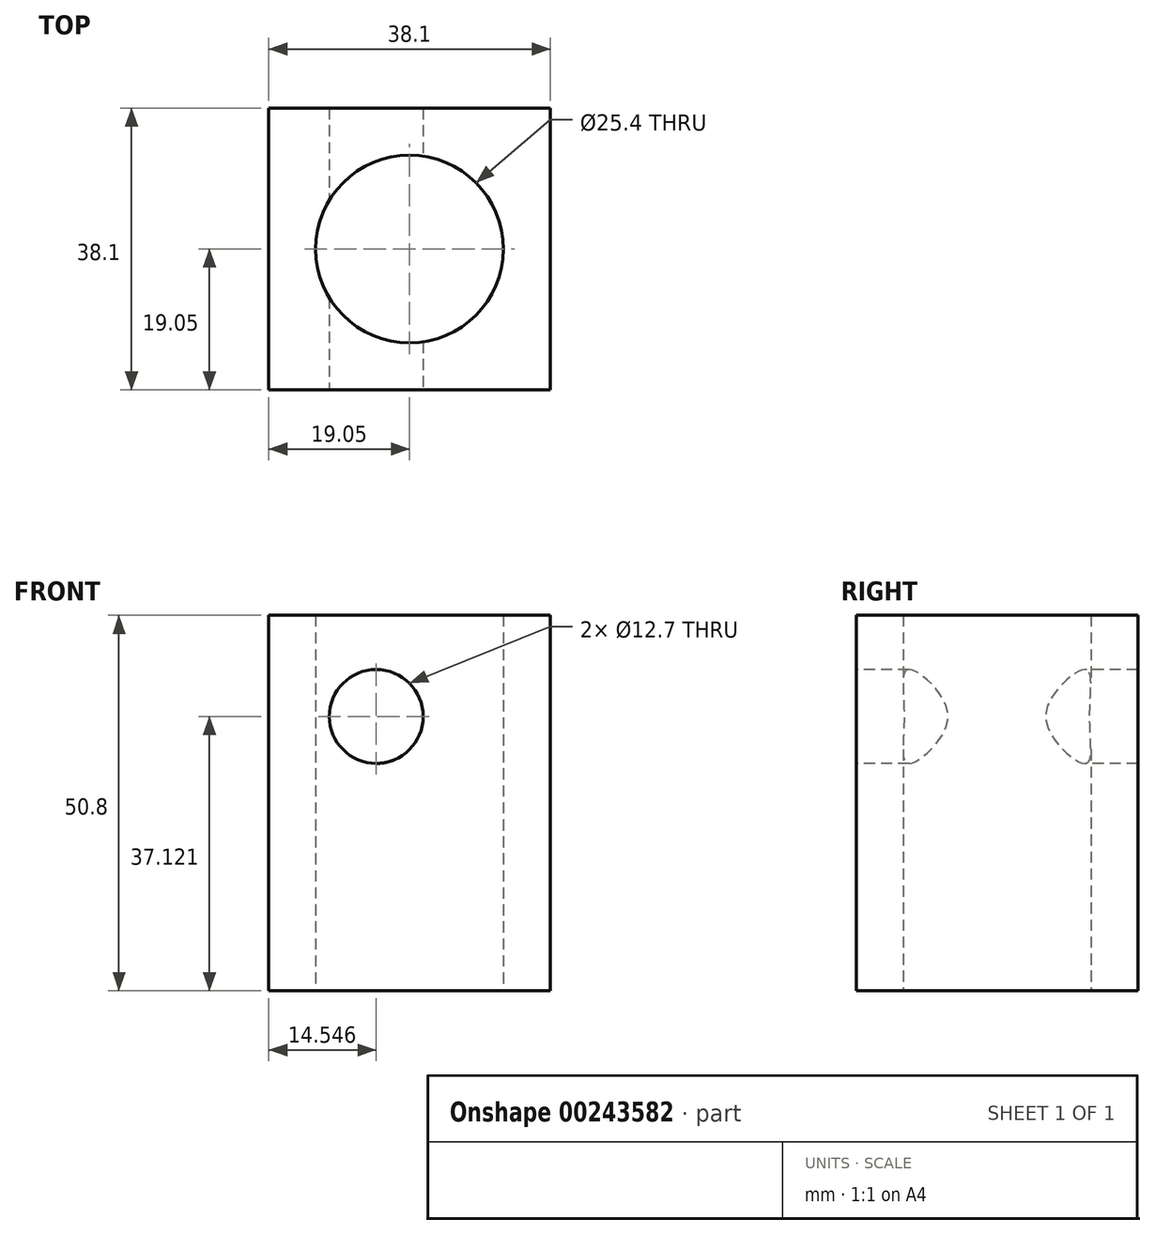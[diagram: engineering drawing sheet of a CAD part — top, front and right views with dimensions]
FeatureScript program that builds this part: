
annotation { "Feature Type Name" : "Feature", "Feature Type Description" : "" }
export const myFeature = defineFeature(function(context is Context, id is Id, definition is map)
    precondition{}
    {
        {
            var Q0;
            Q0=qCreatedBy(makeId("Top.planeOp"),FACE);
            var sketch = newSketch(context, id + "F0", { "sketchPlane" : qUnion([Q0])});
            skLineSegment(sketch, "E0.bottom", {"start": v(-19.05, -19.05) * mm, "end": v(19.05, -19.05) * mm});
            skLineSegment(sketch, "E0.top", {"start": v(-19.05, 19.05) * mm, "end": v(19.05, 19.05) * mm});
            skLineSegment(sketch, "E0.left", {"start": v(-19.05, -19.05) * mm, "end": v(-19.05, 19.05) * mm});
            skLineSegment(sketch, "E0.right", {"start": v(19.05, -19.05) * mm, "end": v(19.05, 19.05) * mm});
            skPoint(sketch, "E0.middle", {"position": v(0, 0) * mm});
            skCircle(sketch, "E1", {"center": v(0, 0) * mm, "radius": 12.7 * mm});
            skSolve(sketch);
        }
        {
            var Q0;
            Q0=makeQuery(id+"F0.imprint","IMPRINT",FACE,{"disambiguationData":[TD([[makeQuery(id+"F0.imprint","IMPRINT",EDGE,{"derivedFrom":sQuery(id+"F0.wireOp",EDGE,"E0.bottom")}),1.0]])]});
            extrude(context, id + "F1", {"entities" : qUnion([Q0]), "depth" : 50.8 * mm});
        }
        {
            var Q0;
            Q0=makeQuery(id+"F1.opExtrude","SWEPT_FACE",FACE,{"disambiguationData":[OSD([sQuery(id+"F0.wireOp",EDGE,"E0.bottom")])]});
            var sketch = newSketch(context, id + "F2", { "sketchPlane" : qUnion([Q0])});
            skCircle(sketch, "E2", {"center": v(-4.5, 37.12) * mm, "radius": 6.35 * mm});
            skSolve(sketch);
        }
        {
            var Q0;
            Q0=makeQuery(id+"F2.imprint","IMPRINT",FACE,{"disambiguationData":[TD([[makeQuery(id+"F2.imprint","IMPRINT",EDGE,{"derivedFrom":sQuery(id+"F2.wireOp",EDGE,"E2")}),1.0]])]});
            var Q1;
            Q1=makeQuery(id+"F1.opExtrude","SWEPT_FACE",FACE,{"disambiguationData":[OSD([sQuery(id+"F0.wireOp",EDGE,"E0.top")])]});
            extrude(context, id + "F3", {"entities" : qUnion([Q0]), "operationType" : NewBodyOperationType.REMOVE, "endBound" : BoundingType.UP_TO_SURFACE, "oppositeDirection" : true, "endBoundEntityFace" : qUnion([Q1]), "depth" : 25.4 * mm});
        }
    });
